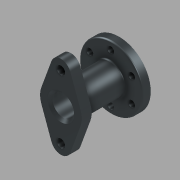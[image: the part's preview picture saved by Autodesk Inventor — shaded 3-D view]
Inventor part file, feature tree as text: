
AUTODESK INVENTOR PART (.ipt)
format: ipt  version: 2020 (Build 240168000, 168)  size: 184,320 bytes
history: native  units: mm
features: sketch x3, other x1, revolve x1, extrude x1, hole x1, pattern_circular x1, chamfer x1, fillet x1
ambient origin geometry x8: Origin, YZ Plane, XZ Plane, XY Plane, X Axis, Y Axis, Z Axis, Center Point
bodies: Body1 (feature_tree)
feature tree (10):
  other  "Sólido1"
  revolve  "Revolución1"  [1 undecoded]
  extrude  "Extrusión1"  Depth=10.0mm
  hole  "Agujero1"  [1 undecoded]
  pattern_circular  "Patrón circular1"  Angle=90.0deg  [1 undecoded]
  chamfer  "Chaflán1"  Distance=12.0mm
  fillet  "Empalme1"  Radius=25.0mm
  sketch  "Boceto1"  dims[d6=20.0mm d8=36.0mm]
  sketch  "Boceto2"  dims[d9=10.0mm d10=76.0mm]
  sketch  "Boceto3"  dims[d11=26.0mm d12=25.0mm d13=90.0deg d14=12.0mm d15=25.0mm d16=38.0mm d17=10.0mm d18=12.0mm d19=0.0mm d20=58.0mm d21=8.0mm d22=6.0mm d23=25.4mm d24=6.35mm d25=90.0deg d26=8.0mm d27=20.594885mm d28=60.0mm d29=360.0deg d31=3.0mm d32=2.0mm d33=45.0deg d34=2.0mm d35=70.0mm d30=0.0625mm]
note: 3 required parameter values undecoded (feature->parameter linkage not recoverable at this tier; creation-order binding heuristic only, values carry confidence <= 0.55)